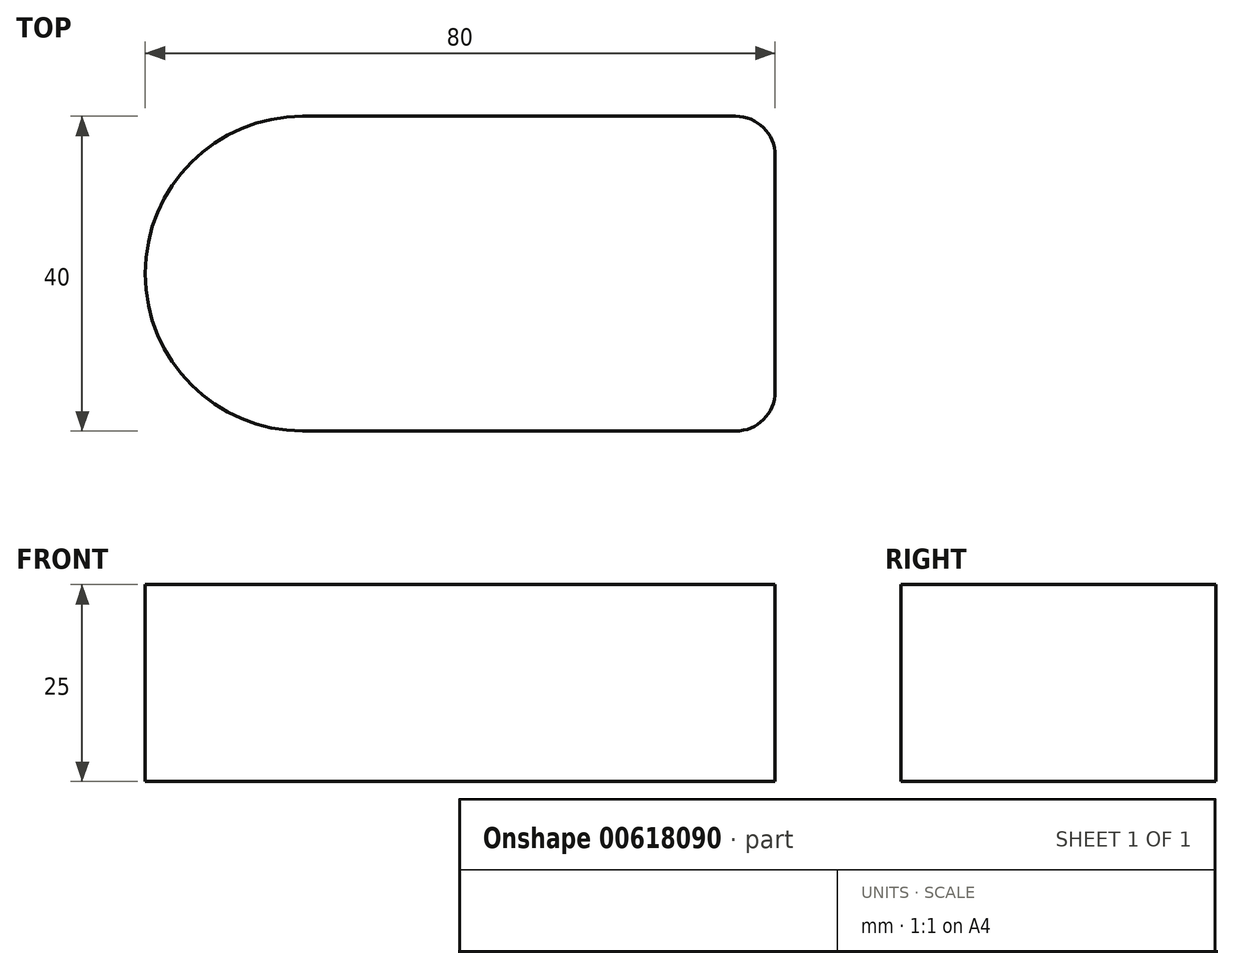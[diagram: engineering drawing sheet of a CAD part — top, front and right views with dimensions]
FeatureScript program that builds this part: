
annotation { "Feature Type Name" : "Feature", "Feature Type Description" : "" }
export const myFeature = defineFeature(function(context is Context, id is Id, definition is map)
    precondition{}
    {
        {
            var Q0;
            Q0=qCreatedBy(makeId("Top.planeOp"),FACE);
            var sketch = newSketch(context, id + "F0", { "sketchPlane" : qUnion([Q0])});
            skLineSegment(sketch, "E0.bottom", {"start": v(0, 0) * mm, "end": v(80, 0) * mm});
            skLineSegment(sketch, "E0.top", {"start": v(0, 40) * mm, "end": v(80, 40) * mm});
            skLineSegment(sketch, "E0.left", {"start": v(0, 0) * mm, "end": v(0, 40) * mm});
            skLineSegment(sketch, "E0.right", {"start": v(80, 0) * mm, "end": v(80, 40) * mm});
            skSolve(sketch);
        }
        {
            var Q0;
            Q0=makeQuery(id+"F0.imprint","IMPRINT",FACE,{"disambiguationData":[TD([[makeQuery(id+"F0.imprint","IMPRINT",EDGE,{"derivedFrom":sQuery(id+"F0.wireOp",EDGE,"E0.bottom")}),1.0]])]});
            extrude(context, id + "F1", {"entities" : qUnion([Q0]), "depth" : 25 * mm, "offsetDistance" : 25 * mm});
        }
        {
            var Q0;
            Q0=makeQuery(id+"F1.opExtrude","SWEPT_EDGE",EDGE,{"disambiguationData":[OSD([sQuery(id+"F0.wireOp",EDGE,"E0.top"),sQuery(id+"F0.wireOp",EDGE,"E0.left")])]});
            var Q1;
            Q1=makeQuery(id+"F1.opExtrude","SWEPT_EDGE",EDGE,{"disambiguationData":[OSD([sQuery(id+"F0.wireOp",EDGE,"E0.bottom"),sQuery(id+"F0.wireOp",EDGE,"E0.left")])]});
            fillet(context, id + "F2", {"entities" : qUnion([Q0, Q1]), "radius" : 20 * mm, "tangentPropagation" : true, "allowEdgeOverflow" : false});
        }
        {
            var Q0;
            Q0=makeQuery(id+"F1.opExtrude","SWEPT_EDGE",EDGE,{"disambiguationData":[OSD([sQuery(id+"F0.wireOp",EDGE,"E0.top"),sQuery(id+"F0.wireOp",EDGE,"E0.right")])]});
            var Q1;
            Q1=makeQuery(id+"F1.opExtrude","SWEPT_EDGE",EDGE,{"disambiguationData":[OSD([sQuery(id+"F0.wireOp",EDGE,"E0.bottom"),sQuery(id+"F0.wireOp",EDGE,"E0.right")])]});
            fillet(context, id + "F3", {"entities" : qUnion([Q0, Q1]), "radius" : 5 * mm, "tangentPropagation" : true, "allowEdgeOverflow" : false});
        }
    });
